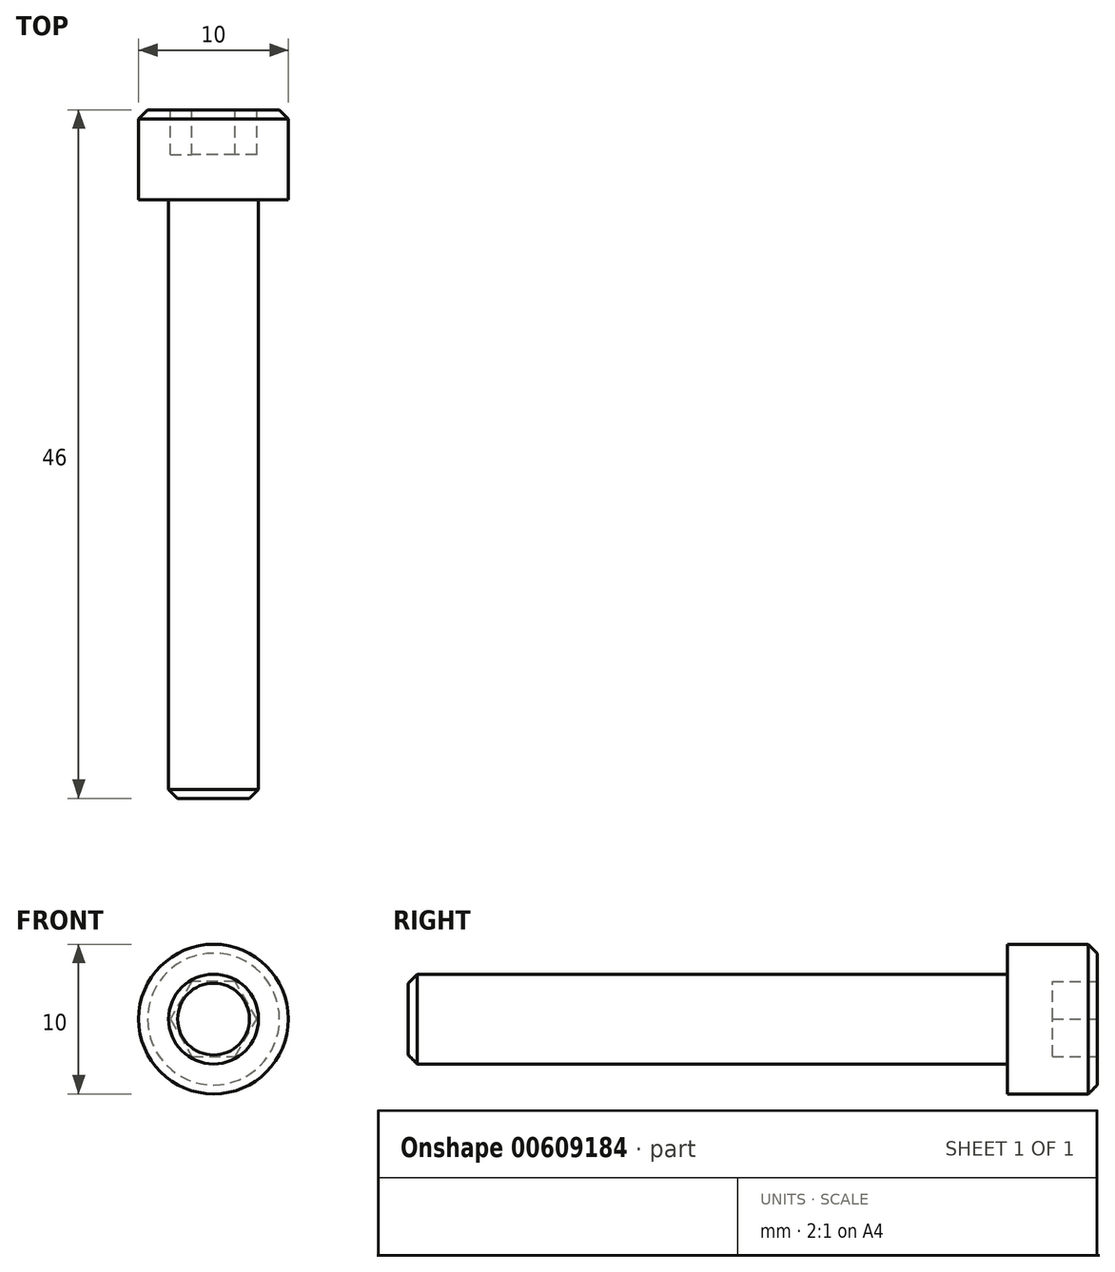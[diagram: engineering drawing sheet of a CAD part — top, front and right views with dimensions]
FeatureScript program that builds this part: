
annotation { "Feature Type Name" : "Feature", "Feature Type Description" : "" }
export const myFeature = defineFeature(function(context is Context, id is Id, definition is map)
    precondition{}
    {
        {
            var Q0;
            Q0=qCreatedBy(makeId("Front.planeOp"),FACE);
            var sketch = newSketch(context, id + "F0", { "sketchPlane" : qUnion([Q0])});
            skCircle(sketch, "E0", {"center": v(0, 0) * mm, "radius": 5 * mm});
            skSolve(sketch);
        }
        {
            var Q0;
            Q0 = qSketchRegion(id + "F0", true);
            extrude(context, id + "F1", {"entities" : qUnion([Q0]), "depth" : 6 * mm, "offsetDistance" : 25 * mm});
        }
        {
            var Q0;
            Q0=makeQuery(id+"F1.opExtrude","CAP_FACE",FACE,{"disambiguationData":[OSD([sQuery(id+"F0.wireOp",EDGE,"E0")])],"isStart":false});
            var sketch = newSketch(context, id + "F2", { "sketchPlane" : qUnion([Q0])});
            skCircle(sketch, "E1", {"center": v(0, 0) * mm, "radius": 3 * mm});
            skSolve(sketch);
        }
        {
            var Q0;
            Q0 = qSketchRegion(id + "F2", true);
            extrude(context, id + "F3", {"entities" : qUnion([Q0]), "operationType" : NewBodyOperationType.ADD, "depth" : 40 * mm, "offsetDistance" : 25 * mm});
        }
        {
            var Q0;
            Q0=makeQuery(id+"F1.opExtrude","CAP_FACE",FACE,{"disambiguationData":[OSD([sQuery(id+"F0.wireOp",EDGE,"E0")])],"isStart":true});
            var sketch = newSketch(context, id + "F4", { "sketchPlane" : qUnion([Q0])});
            skCircle(sketch, "E2.cCircle", {"center": v(0, 0) * mm, "radius": 2.5 * mm, "construction": true});
            skLineSegment(sketch, "E2.0", {"start": v(-1.44, 2.5) * mm, "end": v(1.44, 2.5) * mm});
            skLineSegment(sketch, "E2.1", {"start": v(1.44, 2.5) * mm, "end": v(2.89, 0) * mm});
            skLineSegment(sketch, "E2.2", {"start": v(2.89, 0) * mm, "end": v(1.44, -2.5) * mm});
            skLineSegment(sketch, "E2.3", {"start": v(1.44, -2.5) * mm, "end": v(-1.44, -2.5) * mm});
            skLineSegment(sketch, "E2.4", {"start": v(-1.44, -2.5) * mm, "end": v(-2.89, 0) * mm});
            skLineSegment(sketch, "E2.5", {"start": v(-2.89, 0) * mm, "end": v(-1.44, 2.5) * mm});
            skPoint(sketch, "E2.0.midPoint", {"position": v(0, 2.5) * mm});
            skSolve(sketch);
        }
        {
            var Q0;
            Q0 = qSketchRegion(id + "F4", true);
            extrude(context, id + "F5", {"entities" : qUnion([Q0]), "operationType" : NewBodyOperationType.REMOVE, "oppositeDirection" : true, "depth" : 3 * mm, "offsetDistance" : 25 * mm});
        }
        {
            var Q0;
            Q0=makeQuery(id+"F1.opExtrude","CAP_EDGE",EDGE,{"disambiguationData":[OSD([sQuery(id+"F0.wireOp",EDGE,"E0")])],"isStart":true});
            var Q1;
            Q1=makeQuery(id+"F3.opExtrude","CAP_EDGE",EDGE,{"disambiguationData":[OSD([sQuery(id+"F2.wireOp",EDGE,"E1")])],"isStart":false});
            chamfer(context, id + "F6", {"entities" : qUnion([Q0, Q1]), "width" : 0.6 * mm, "tangentPropagation" : true});
        }
    });
